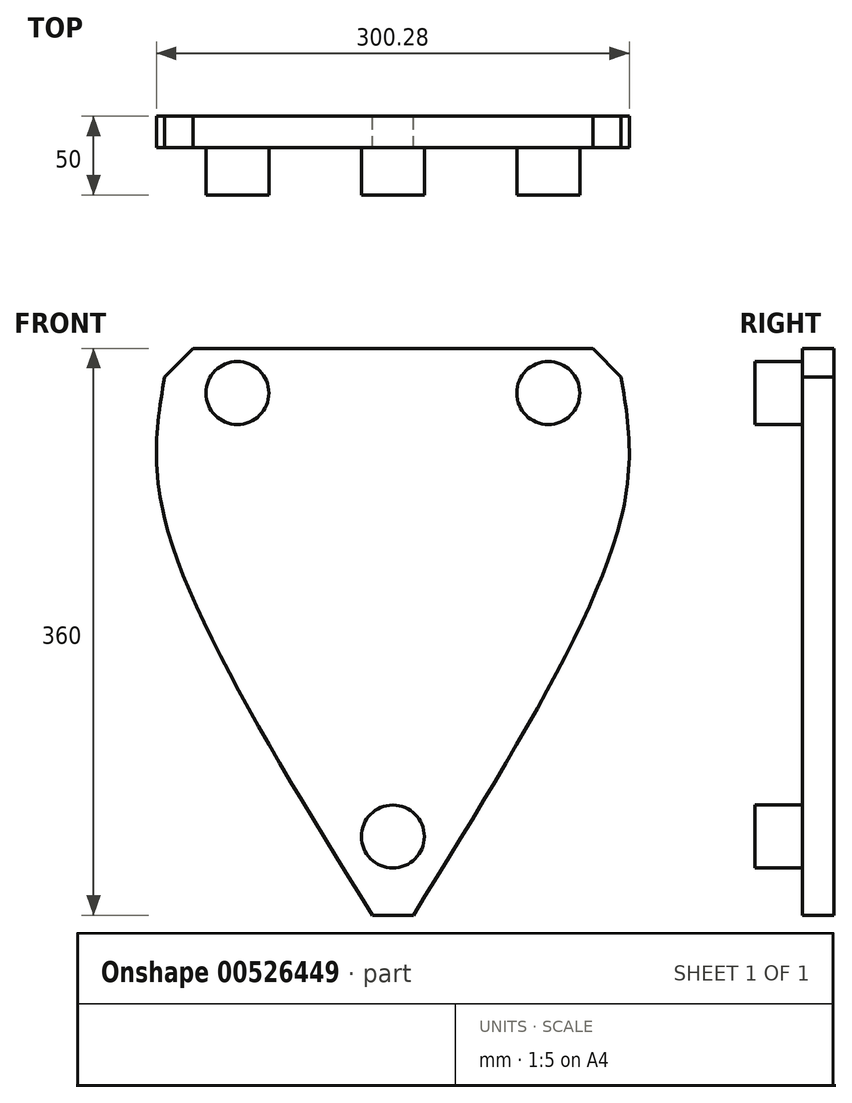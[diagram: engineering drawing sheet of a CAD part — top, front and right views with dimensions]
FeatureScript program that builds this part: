
annotation { "Feature Type Name" : "Feature", "Feature Type Description" : "" }
export const myFeature = defineFeature(function(context is Context, id is Id, definition is map)
    precondition{}
    {
        {
            var Q0;
            Q0=qCreatedBy(makeId("Front.planeOp"),FACE);
            var sketch = newSketch(context, id + "F0", { "sketchPlane" : qUnion([Q0])});
            skLineSegment(sketch, "E0", {"start": v(132, -252) * mm, "end": v(158, -252) * mm});
            skLineSegment(sketch, "E1", {"start": v(0, 0) * mm, "end": v(0, 90) * mm});
            skLineSegment(sketch, "E2", {"start": v(290, 0) * mm, "end": v(290, 90) * mm});
            skLineSegment(sketch, "E3", {"start": v(18, 108) * mm, "end": v(272, 108) * mm});
            skLineSegment(sketch, "E4", {"start": v(18, 108) * mm, "end": v(0, 90) * mm});
            skLineSegment(sketch, "E5", {"start": v(272, 108) * mm, "end": v(290, 90) * mm});
            skLineSegment(sketch, "E6", {"start": v(0, 90) * mm, "end": v(0, 0) * mm});
            skLineSegment(sketch, "E7", {"start": v(290, 90) * mm, "end": v(290, 0) * mm});
            skFitSpline(sketch, "E8", {"points": [v(0, 90) * mm, v(0, 0) * mm, v(132, -252) * mm], "startDerivative": vector(-37.12, -224.14) * mm, "endDerivative": vector(272.25, -439.74) * mm});
            skFitSpline(sketch, "E9", {"points": [v(290, 90) * mm, v(290, 0) * mm, v(158, -252) * mm], "startDerivative": vector(37.12, -224.14) * mm, "endDerivative": vector(-272.25, -439.74) * mm});
            skSolve(sketch);
        }
        {
            var Q0;
            Q0 = qSketchRegion(id + "F0", true);
            extrude(context, id + "F1", {"entities" : qUnion([Q0]), "depth" : 20 * mm, "offsetDistance" : 25 * mm});
        }
        {
            var Q0;
            Q0=makeQuery(id+"F1.opExtrude","CAP_FACE",FACE,{"disambiguationData":[OSD([sQuery(id+"F0.wireOp",EDGE,"E0"),sQuery(id+"F0.wireOp",EDGE,"E3"),sQuery(id+"F0.wireOp",EDGE,"E4"),sQuery(id+"F0.wireOp",EDGE,"E5"),sQuery(id+"F0.wireOp",EDGE,"E6"),sQuery(id+"F0.wireOp",EDGE,"E7"),sQuery(id+"F0.wireOp",EDGE,"E8"),sQuery(id+"F0.wireOp",EDGE,"E9")])],"isStart":false});
            var sketch = newSketch(context, id + "F2", { "sketchPlane" : qUnion([Q0])});
            skCircle(sketch, "E10", {"center": v(46.28, 79.72) * mm, "radius": 20 * mm});
            skCircle(sketch, "E11", {"center": v(243.72, 79.72) * mm, "radius": 20 * mm});
            skCircle(sketch, "E12", {"center": v(145, -202) * mm, "radius": 20 * mm});
            skPoint(sketch, "E13.orphan", {"position": v(145, -252) * mm});
            skSolve(sketch);
        }
        {
            var Q0;
            Q0 = qSketchRegion(id + "F2", true);
            extrude(context, id + "F3", {"entities" : qUnion([Q0]), "operationType" : NewBodyOperationType.ADD, "depth" : 30 * mm, "offsetDistance" : 25 * mm});
        }
    });
